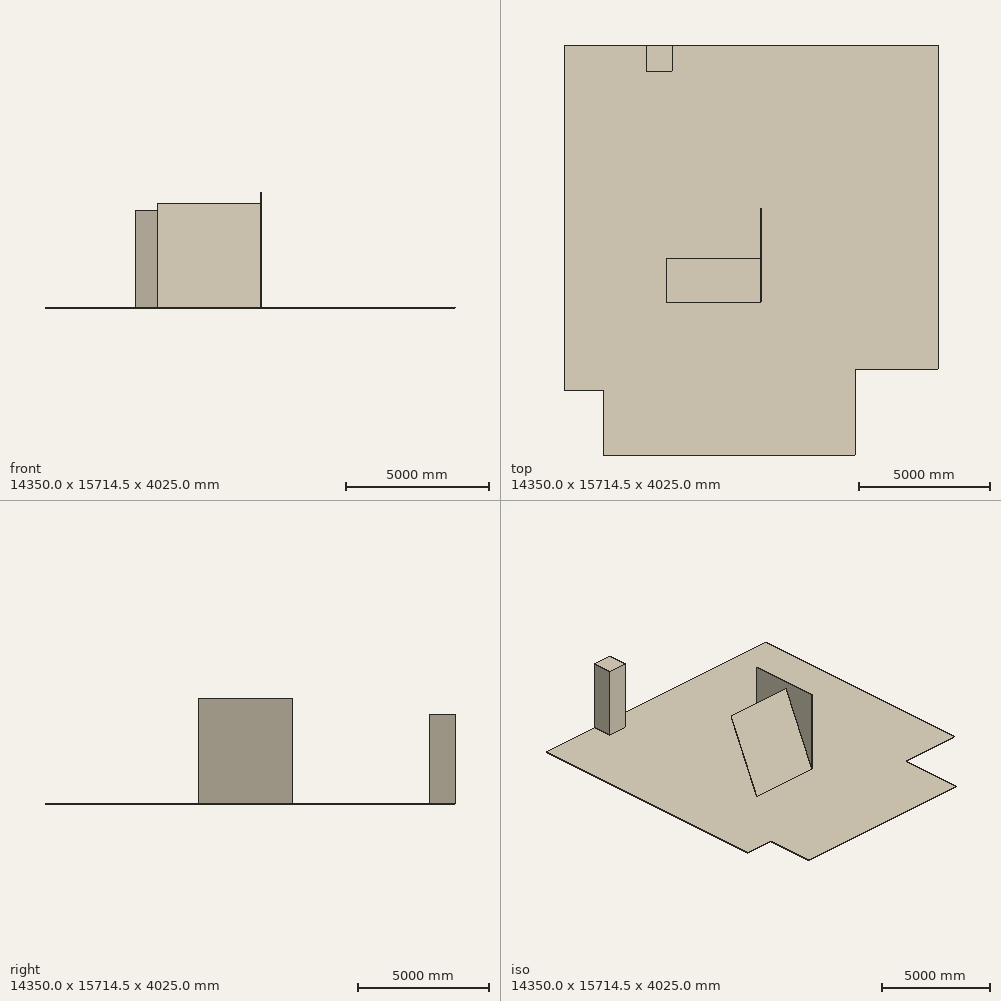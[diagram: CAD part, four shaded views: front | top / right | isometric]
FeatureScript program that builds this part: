
annotation { "Feature Type Name" : "Feature", "Feature Type Description" : "" }
export const myFeature = defineFeature(function(context is Context, id is Id, definition is map)
    precondition{}
    {
        {
            var Q0;
            Q0=qCreatedBy(makeId("Top.planeOp"),FACE);
            var sketch = newSketch(context, id + "F0", { "sketchPlane" : qUnion([Q0])});
            skLineSegment(sketch, "E0.bottom", {"start": v(-5920.52, 9833.93) * mm, "end": v(8429.48, 9833.93) * mm});
            skLineSegment(sketch, "E0.top", {"start": v(-4420.52, -5866.07) * mm, "end": v(5229.48, -5866.07) * mm});
            skLineSegment(sketch, "E0.left", {"start": v(-5920.52, 9833.93) * mm, "end": v(-5920.52, -3366.07) * mm});
            skLineSegment(sketch, "E0.right", {"start": v(8429.48, 9833.93) * mm, "end": v(8429.48, -2566.07) * mm});
            skLineSegment(sketch, "E1.bottom", {"start": v(-5920.52, -3366.07) * mm, "end": v(-4420.52, -3366.07) * mm});
            skLineSegment(sketch, "E1.right", {"start": v(-4420.52, -3366.07) * mm, "end": v(-4420.52, -5866.07) * mm});
            skLineSegment(sketch, "E2.bottom", {"start": v(8429.48, -2566.07) * mm, "end": v(5229.48, -2566.07) * mm});
            skLineSegment(sketch, "E2.right", {"start": v(5229.48, -2566.07) * mm, "end": v(5229.48, -5866.07) * mm});
            skSolve(sketch);
        }
        {
            var Q0;
            Q0 = qSketchRegion(id + "F0", true);
            extrude(context, id + "F1", {"entities" : qUnion([Q0]), "depth" : -25 * mm, "offsetDistance" : 25 * mm});
        }
        {
            var Q0;
            Q0=qCreatedBy(makeId("Right.planeOp"),FACE);
            var sketch = newSketch(context, id + "F2", { "sketchPlane" : qUnion([Q0])});
            skLineSegment(sketch, "E3.bottom", {"start": v(908.45, 3400) * mm, "end": v(-91.55, 3400) * mm});
            skLineSegment(sketch, "E3.top", {"start": v(908.45, 0) * mm, "end": v(-91.55, 0) * mm});
            skLineSegment(sketch, "E3.left", {"start": v(908.45, 3400) * mm, "end": v(908.45, 0) * mm});
            skLineSegment(sketch, "E3.right", {"start": v(-91.55, 3400) * mm, "end": v(-91.55, 0) * mm});
            skSolve(sketch);
        }
        {
            var Q0;
            Q0=makeQuery(id+"F2.imprint","IMPRINT",FACE,{"disambiguationData":[TD([[makeQuery(id+"F2.imprint","IMPRINT",EDGE,{"derivedFrom":sQuery(id+"F2.wireOp",EDGE,"E3.bottom")}),1.0]])]});
            extrude(context, id + "F3", {"entities" : qUnion([Q0]), "depth" : 1000 * mm, "offsetDistance" : 25 * mm});
        }
        {
            var Q0;
            Q0=makeQuery(id+"F3.opExtrude","SWEPT_BODY",BODY,{"disambiguationData":[OSD([sQuery(id+"F2.wireOp",EDGE,"E3.bottom"),sQuery(id+"F2.wireOp",EDGE,"E3.top"),sQuery(id+"F2.wireOp",EDGE,"E3.left"),sQuery(id+"F2.wireOp",EDGE,"E3.right")])]});
            transform(context, id + "F4", {"entities" : qUnion([Q0]), "transformType" : TransformType.TRANSLATION_3D, "dx" : -2760 * mm, "dy" : 8940 * mm, "dz" : 0 * mm, "makeCopy" : false});
        }
        {
            var Q0;
            Q0=qCreatedBy(makeId("Front.planeOp"),FACE);
            var sketch = newSketch(context, id + "F5", { "sketchPlane" : qUnion([Q0])});
            skLineSegment(sketch, "E4.bottom", {"start": v(-1987.2, 4000) * mm, "end": v(1612.8, 4000) * mm});
            skLineSegment(sketch, "E4.top", {"start": v(-1987.2, 0) * mm, "end": v(1612.8, 0) * mm});
            skLineSegment(sketch, "E4.left", {"start": v(-1987.2, 4000) * mm, "end": v(-1987.2, 0) * mm});
            skLineSegment(sketch, "E4.right", {"start": v(1612.8, 4000) * mm, "end": v(1612.8, 0) * mm});
            skSolve(sketch);
        }
        {
            var Q0;
            Q0 = qSketchRegion(id + "F5", true);
            extrude(context, id + "F6", {"entities" : qUnion([Q0]), "depth" : 15 * mm, "offsetDistance" : 25 * mm});
        }
        {
            var Q0;
            Q0=makeQuery(id+"F6.opExtrude","SWEPT_BODY",BODY,{"disambiguationData":[OSD([sQuery(id+"F5.wireOp",EDGE,"E4.bottom"),sQuery(id+"F5.wireOp",EDGE,"E4.top"),sQuery(id+"F5.wireOp",EDGE,"E4.left"),sQuery(id+"F5.wireOp",EDGE,"E4.right")])]});
            var Q1;
            Q1=makeQuery(id+"F6.opExtrude","CAP_EDGE",EDGE,{"disambiguationData":[OSD([sQuery(id+"F5.wireOp",EDGE,"E4.top")])],"isStart":false});
            transform(context, id + "F7", {"entities" : qUnion([Q0]), "transformType" : TransformType.ROTATION, "transformAxis" : qUnion([Q1]), "angle" : 25 * degree, "oppositeDirection" : true, "makeCopy" : false});
        }
        {
            var Q0;
            Q0=makeQuery(id+"F6.opExtrude","SWEPT_BODY",BODY,{"disambiguationData":[OSD([sQuery(id+"F5.wireOp",EDGE,"E4.bottom"),sQuery(id+"F5.wireOp",EDGE,"E4.top"),sQuery(id+"F5.wireOp",EDGE,"E4.left"),sQuery(id+"F5.wireOp",EDGE,"E4.right")])]});
            var Q1;
            Q1=makeQuery(id+"F6.opExtrude","CAP_EDGE",EDGE,{"disambiguationData":[OSD([sQuery(id+"F5.wireOp",EDGE,"E4.top")])],"isStart":false});
            transform(context, id + "F8", {"entities" : qUnion([Q0]), "transformType" : TransformType.ROTATION, "transformAxis" : qUnion([Q1]), "angle" : 25 * degree, "makeCopy" : true});
        }
        {
            var Q0;
            Q0=makeQuery(id+"F8.opPattern","COPY",BODY,{"derivedFrom":makeQuery(id+"F6.opExtrude","SWEPT_BODY",BODY,{"disambiguationData":[OSD([sQuery(id+"F5.wireOp",EDGE,"E4.bottom"),sQuery(id+"F5.wireOp",EDGE,"E4.top"),sQuery(id+"F5.wireOp",EDGE,"E4.left"),sQuery(id+"F5.wireOp",EDGE,"E4.right")])]}),"instanceName":"1"});
            var Q1;
            Q1=makeQuery(id+"F8.opPattern","COPY",EDGE,{"derivedFrom":makeQuery(id+"F6.opExtrude","CAP_EDGE",EDGE,{"disambiguationData":[OSD([sQuery(id+"F5.wireOp",EDGE,"E4.right")])],"isStart":false}),"instanceName":"1"});
            transform(context, id + "F9", {"entities" : qUnion([Q0]), "transformType" : TransformType.ROTATION, "transformAxis" : qUnion([Q1]), "angle" : 90 * degree, "makeCopy" : false});
        }
    });
